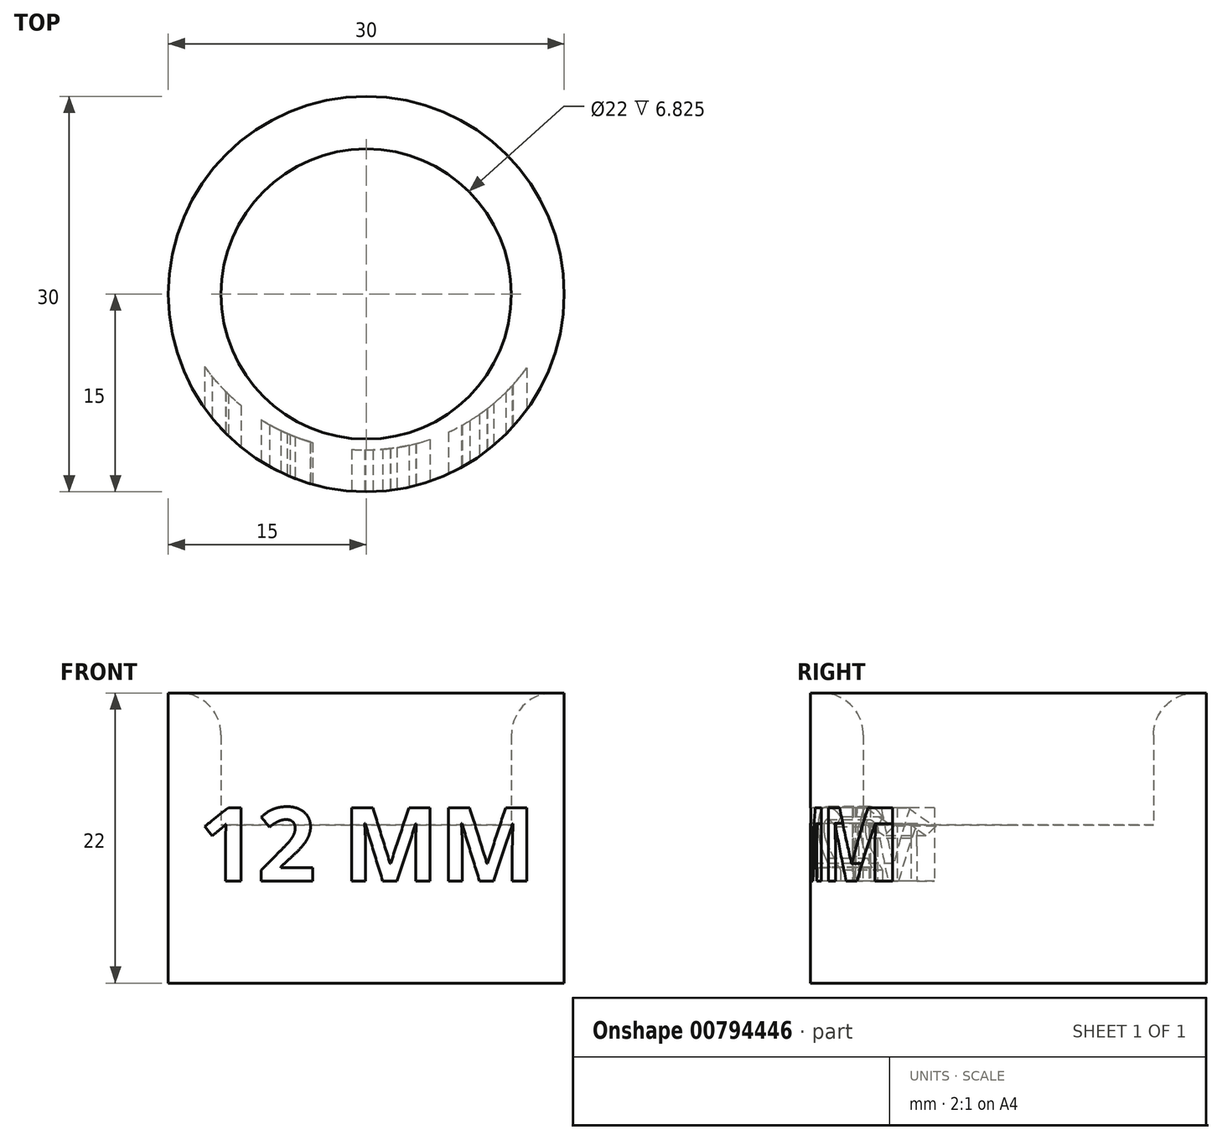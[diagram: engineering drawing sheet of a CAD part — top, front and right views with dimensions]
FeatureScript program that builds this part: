
annotation { "Feature Type Name" : "Feature", "Feature Type Description" : "" }
export const myFeature = defineFeature(function(context is Context, id is Id, definition is map)
    precondition{}
    {
        {
            var Q0;
            Q0=qCreatedBy(makeId("Top.planeOp"),FACE);
            var sketch = newSketch(context, id + "F0", { "sketchPlane" : qUnion([Q0])});
            skCircle(sketch, "E0", {"center": v(0, 0) * mm, "radius": 11 * mm});
            skCircle(sketch, "E1", {"center": v(0, 0) * mm, "radius": 15 * mm});
            skSolve(sketch);
        }
        {
            var Q0;
            Q0 = qSketchRegion(id + "F0", true);
            extrude(context, id + "F1", {"entities" : qUnion([Q0]), "depth" : 10 * mm, "offsetDistance" : 25.4 * mm});
        }
        {
            var Q0;
            Q0=makeQuery(id+"F1.opExtrude","CAP_FACE",FACE,{"disambiguationData":[OSD([sQuery(id+"F0.wireOp",EDGE,"E0"),sQuery(id+"F0.wireOp",EDGE,"E1")])],"isStart":true});
            var sketch = newSketch(context, id + "F2", { "sketchPlane" : qUnion([Q0])});
            skCircle(sketch, "E2.0", {"center": v(0, 0) * mm, "radius": 15 * mm});
            skSolve(sketch);
        }
        {
            var Q0;
            Q0=makeQuery(id+"F2.imprint","IMPRINT",FACE,{"disambiguationData":[TD([[makeQuery(id+"F2.imprint","IMPRINT",EDGE,{"derivedFrom":sQuery(id+"F2.wireOp",EDGE,"E2.0")}),-1.0]])]});
            var Q1;
            Q1=makeQuery(id+"F2.imprint","IMPRINT",FACE,{"disambiguationData":[TD([[makeQuery(id+"F2.imprint","IMPRINT",EDGE,{"derivedFrom":makeQuery(id+"F1.opExtrude","CAP_EDGE",EDGE,{"disambiguationData":[OSD([sQuery(id+"F0.wireOp",EDGE,"E0")])],"isStart":true})}),-1.0]])]});
            extrude(context, id + "F3", {"entities" : qUnion([Q0, Q1]), "operationType" : NewBodyOperationType.ADD, "depth" : 12 * mm, "offsetDistance" : 25.4 * mm});
        }
        {
            var Q0;
            Q0=makeQuery(id+"F1.opExtrude","CAP_EDGE",EDGE,{"disambiguationData":[OSD([sQuery(id+"F0.wireOp",EDGE,"E0")])],"isStart":false});
            fillet(context, id + "F4", {"entities" : qUnion([Q0]), "radius" : 3.17 * mm, "tangentPropagation" : true, "allowEdgeOverflow" : false});
        }
        {
            var Q0;
            Q0=qCreatedBy(makeId("Front.planeOp"),FACE);
            cPlane(context, id + "F5", {"entities" : qUnion([Q0]), "cplaneType" : CPlaneType.OFFSET, "offset" : 15 * mm, "width" : 152.4 * mm, "height" : 152.4 * mm});
        }
        {
            var Q0;
            Q0=qCreatedBy(id+"F5.planeOp",FACE);
            var sketch = newSketch(context, id + "F6", { "sketchPlane" : qUnion([Q0])});
            skText(sketch, "E3", { "text": "12 MM", "fontName": "OpenSans-Bold.ttf"});
            const initialGuessF6  = {"E3": [-0.0127, -0.00425, 1, 0, 0.0056]};
            skSetInitialGuess(sketch, initialGuessF6);
            skSolve(sketch);
        }
        {
            var Q0;
            Q0 = qSketchRegion(id + "F6", true);
            var Q1;
            Q1=makeQuery(id+"F3.boolean.opBoolean","MERGE",FACE,{"derivedFrom":[makeQuery(id+"F1.opExtrude","SWEPT_FACE",FACE,{"disambiguationData":[OSD([sQuery(id+"F0.wireOp",EDGE,"E1")])]}),makeQuery(id+"F3.opExtrude","SWEPT_FACE",FACE,{"disambiguationData":[OSD([sQuery(id+"F2.wireOp",EDGE,"E2.0")])]})]});
            extrude(context, id + "F7", {"entities" : qUnion([Q0]), "operationType" : NewBodyOperationType.REMOVE, "endBound" : BoundingType.UP_TO_SURFACE, "oppositeDirection" : true, "depth" : 13.97 * mm, "endBoundEntityFace" : qUnion([Q1]), "hasOffset" : true, "offsetDistance" : -3.17 * mm});
        }
    });
